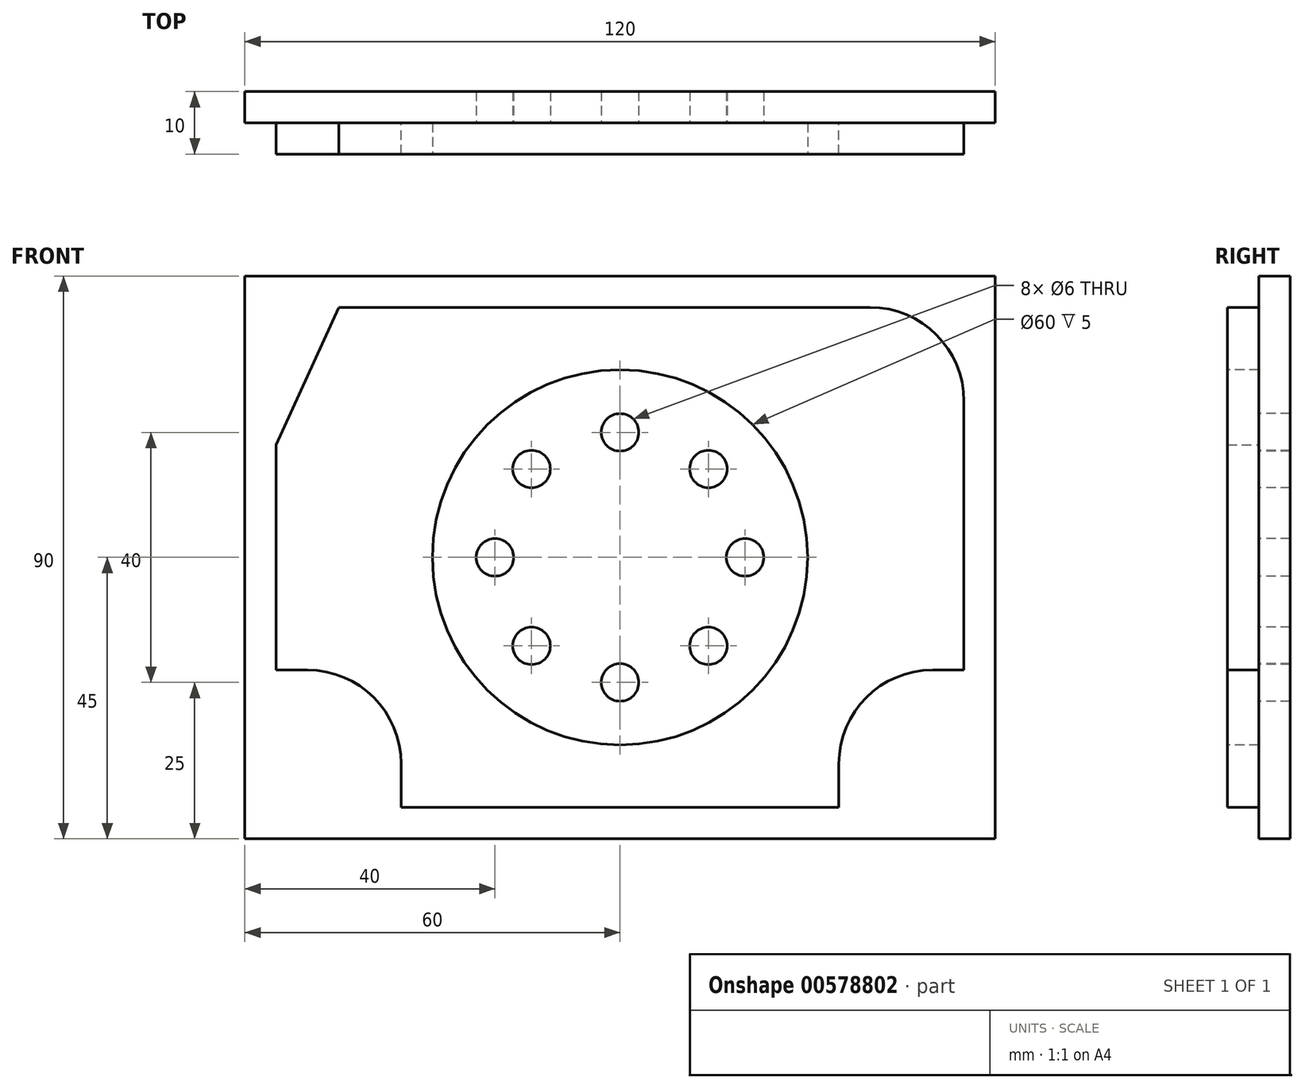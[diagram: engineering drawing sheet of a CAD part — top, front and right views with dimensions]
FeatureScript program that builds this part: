
annotation { "Feature Type Name" : "Feature", "Feature Type Description" : "" }
export const myFeature = defineFeature(function(context is Context, id is Id, definition is map)
    precondition{}
    {
        {
            var Q0;
            Q0=qCreatedBy(makeId("Front.planeOp"),FACE);
            var sketch = newSketch(context, id + "F0", { "sketchPlane" : qUnion([Q0])});
            skLineSegment(sketch, "E0.bottom", {"start": v(-60, 45) * mm, "end": v(60, 45) * mm});
            skLineSegment(sketch, "E0.top", {"start": v(-60, -45) * mm, "end": v(60, -45) * mm});
            skLineSegment(sketch, "E0.left", {"start": v(-60, 45) * mm, "end": v(-60, -45) * mm});
            skLineSegment(sketch, "E0.right", {"start": v(60, 45) * mm, "end": v(60, -45) * mm});
            skPoint(sketch, "E0.middle", {"position": v(0, 0) * mm});
            skSolve(sketch);
        }
        {
            var Q0;
            Q0=makeQuery(id+"F0.imprint","IMPRINT",FACE,{"disambiguationData":[TD([[makeQuery(id+"F0.imprint","IMPRINT",EDGE,{"derivedFrom":sQuery(id+"F0.wireOp",EDGE,"E0.bottom")}),-1.0]])]});
            extrude(context, id + "F1", {"entities" : qUnion([Q0]), "depth" : 5 * mm, "offsetDistance" : 25 * mm});
        }
        {
            var Q0;
            Q0=makeQuery(id+"F1.opExtrude","CAP_FACE",FACE,{"disambiguationData":[OSD([sQuery(id+"F0.wireOp",EDGE,"E0.bottom"),sQuery(id+"F0.wireOp",EDGE,"E0.top"),sQuery(id+"F0.wireOp",EDGE,"E0.left"),sQuery(id+"F0.wireOp",EDGE,"E0.right")])],"isStart":false});
            var sketch = newSketch(context, id + "F2", { "sketchPlane" : qUnion([Q0])});
            skLineSegment(sketch, "E1", {"start": v(-55, -18) * mm, "end": v(-55, 18) * mm});
            skLineSegment(sketch, "E2", {"start": v(-55, 18) * mm, "end": v(-45, 40) * mm});
            skLineSegment(sketch, "E3", {"start": v(-45, 40) * mm, "end": v(40, 40) * mm});
            skLineSegment(sketch, "E4", {"start": v(55, 25) * mm, "end": v(55, -18) * mm});
            skLineSegment(sketch, "E5", {"start": v(35, -40) * mm, "end": v(-35, -40) * mm});
            skPoint(sketch, "E6.visualSharp", {"position": v(55, 40) * mm});
            skArc(sketch, "E6.filletArc", {"start": v(55, 25) * mm, "mid": v(50.6, 35.6) * mm, "end": v(40, 40) * mm});
            skLineSegment(sketch, "E7", {"start": v(-35, -40) * mm, "end": v(-35, -33) * mm});
            skLineSegment(sketch, "E8", {"start": v(-55, -18) * mm, "end": v(-50, -18) * mm});
            skArc(sketch, "E9", {"start": v(-35, -33) * mm, "mid": v(-39.4, -22.4) * mm, "end": v(-50, -18) * mm});
            skLineSegment(sketch, "E10", {"start": v(35, -40) * mm, "end": v(35, -33) * mm});
            skLineSegment(sketch, "E11", {"start": v(55, -18) * mm, "end": v(50, -18) * mm});
            skArc(sketch, "E12", {"start": v(50, -18) * mm, "mid": v(39.4, -22.4) * mm, "end": v(35, -33) * mm});
            skSolve(sketch);
        }
        {
            var Q0;
            Q0=makeQuery(id+"F2.imprint","IMPRINT",FACE,{"disambiguationData":[TD([[makeQuery(id+"F2.imprint","IMPRINT",EDGE,{"derivedFrom":sQuery(id+"F2.wireOp",EDGE,"E1")}),-1.0]])]});
            extrude(context, id + "F3", {"entities" : qUnion([Q0]), "operationType" : NewBodyOperationType.ADD, "depth" : 5 * mm, "offsetDistance" : 25 * mm});
        }
        {
            var Q0;
            Q0=makeQuery(id+"F3.opExtrude","CAP_FACE",FACE,{"disambiguationData":[OSD([sQuery(id+"F2.wireOp",EDGE,"E1"),sQuery(id+"F2.wireOp",EDGE,"E2"),sQuery(id+"F2.wireOp",EDGE,"E3"),sQuery(id+"F2.wireOp",EDGE,"E4"),sQuery(id+"F2.wireOp",EDGE,"E5"),sQuery(id+"F2.wireOp",EDGE,"vpOuNTtm-nmTs-lWEv-Da7O-z1g3FIr5LAAq"),sQuery(id+"F2.wireOp",EDGE,"bwUYAi5J-tQoA-iiAx-xwBu-JcA3UBjWhWz0")])],"isStart":false});
            var sketch = newSketch(context, id + "F4", { "sketchPlane" : qUnion([Q0])});
            skCircle(sketch, "E13", {"center": v(0, 0) * mm, "radius": 30 * mm});
            skSolve(sketch);
        }
        {
            var Q0;
            Q0=makeQuery(id+"F4.imprint","IMPRINT",FACE,{"disambiguationData":[TD([[makeQuery(id+"F4.imprint","IMPRINT",EDGE,{"derivedFrom":sQuery(id+"F4.wireOp",EDGE,"E13")}),1.0]])]});
            extrude(context, id + "F5", {"entities" : qUnion([Q0]), "operationType" : NewBodyOperationType.REMOVE, "oppositeDirection" : true, "depth" : 5 * mm, "offsetDistance" : 25 * mm});
        }
        {
            var Q0;
            Q0=makeQuery(id+"F5.boolean.opBoolean","COPY",FACE,{"derivedFrom":makeQuery(id+"F5.opExtrude","CAP_FACE",FACE,{"disambiguationData":[OSD([sQuery(id+"F4.wireOp",EDGE,"E13")])],"isStart":false})});
            var sketch = newSketch(context, id + "F6", { "sketchPlane" : qUnion([Q0])});
            skCircle(sketch, "E14", {"center": v(0, 0) * mm, "radius": 20 * mm, "construction": true});
            skCircle(sketch, "E15", {"center": v(-20, 0) * mm, "radius": 3 * mm});
            skCircle(sketch, "E16", {"center": v(20, 0) * mm, "radius": 3 * mm});
            skCircle(sketch, "E17", {"center": v(0, 20) * mm, "radius": 3 * mm});
            skCircle(sketch, "E18", {"center": v(0, -20) * mm, "radius": 3 * mm});
            skCircle(sketch, "E19", {"center": v(-14.14, 14.14) * mm, "radius": 3 * mm});
            skCircle(sketch, "E20", {"center": v(14.14, 14.14) * mm, "radius": 3 * mm});
            skCircle(sketch, "E21", {"center": v(-14.14, -14.14) * mm, "radius": 3 * mm});
            skCircle(sketch, "E22", {"center": v(14.14, -14.14) * mm, "radius": 3 * mm});
            skSolve(sketch);
        }
        {
            var Q0;
            Q0=makeQuery(id+"F6.imprint","IMPRINT",FACE,{"disambiguationData":[TD([[makeQuery(id+"F6.imprint","IMPRINT",EDGE,{"derivedFrom":sQuery(id+"F6.wireOp",EDGE,"E19")}),1.0]])]});
            var Q1;
            Q1=makeQuery(id+"F6.imprint","IMPRINT",FACE,{"disambiguationData":[TD([[makeQuery(id+"F6.imprint","IMPRINT",EDGE,{"derivedFrom":sQuery(id+"F6.wireOp",EDGE,"E17")}),1.0]])]});
            var Q2;
            Q2=makeQuery(id+"F6.imprint","IMPRINT",FACE,{"disambiguationData":[TD([[makeQuery(id+"F6.imprint","IMPRINT",EDGE,{"derivedFrom":sQuery(id+"F6.wireOp",EDGE,"E20")}),1.0]])]});
            var Q3;
            Q3=makeQuery(id+"F6.imprint","IMPRINT",FACE,{"disambiguationData":[TD([[makeQuery(id+"F6.imprint","IMPRINT",EDGE,{"derivedFrom":sQuery(id+"F6.wireOp",EDGE,"E16")}),1.0]])]});
            var Q4;
            Q4=makeQuery(id+"F6.imprint","IMPRINT",FACE,{"disambiguationData":[TD([[makeQuery(id+"F6.imprint","IMPRINT",EDGE,{"derivedFrom":sQuery(id+"F6.wireOp",EDGE,"E22")}),1.0]])]});
            var Q5;
            Q5=makeQuery(id+"F6.imprint","IMPRINT",FACE,{"disambiguationData":[TD([[makeQuery(id+"F6.imprint","IMPRINT",EDGE,{"derivedFrom":sQuery(id+"F6.wireOp",EDGE,"E18")}),1.0]])]});
            var Q6;
            Q6=makeQuery(id+"F6.imprint","IMPRINT",FACE,{"disambiguationData":[TD([[makeQuery(id+"F6.imprint","IMPRINT",EDGE,{"derivedFrom":sQuery(id+"F6.wireOp",EDGE,"E21")}),1.0]])]});
            var Q7;
            Q7=makeQuery(id+"F6.imprint","IMPRINT",FACE,{"disambiguationData":[TD([[makeQuery(id+"F6.imprint","IMPRINT",EDGE,{"derivedFrom":sQuery(id+"F6.wireOp",EDGE,"E15")}),1.0]])]});
            extrude(context, id + "F7", {"entities" : qUnion([Q0, Q1, Q2, Q3, Q4, Q5, Q6, Q7]), "operationType" : NewBodyOperationType.REMOVE, "oppositeDirection" : true, "depth" : 5 * mm, "offsetDistance" : 25 * mm});
        }
    });
